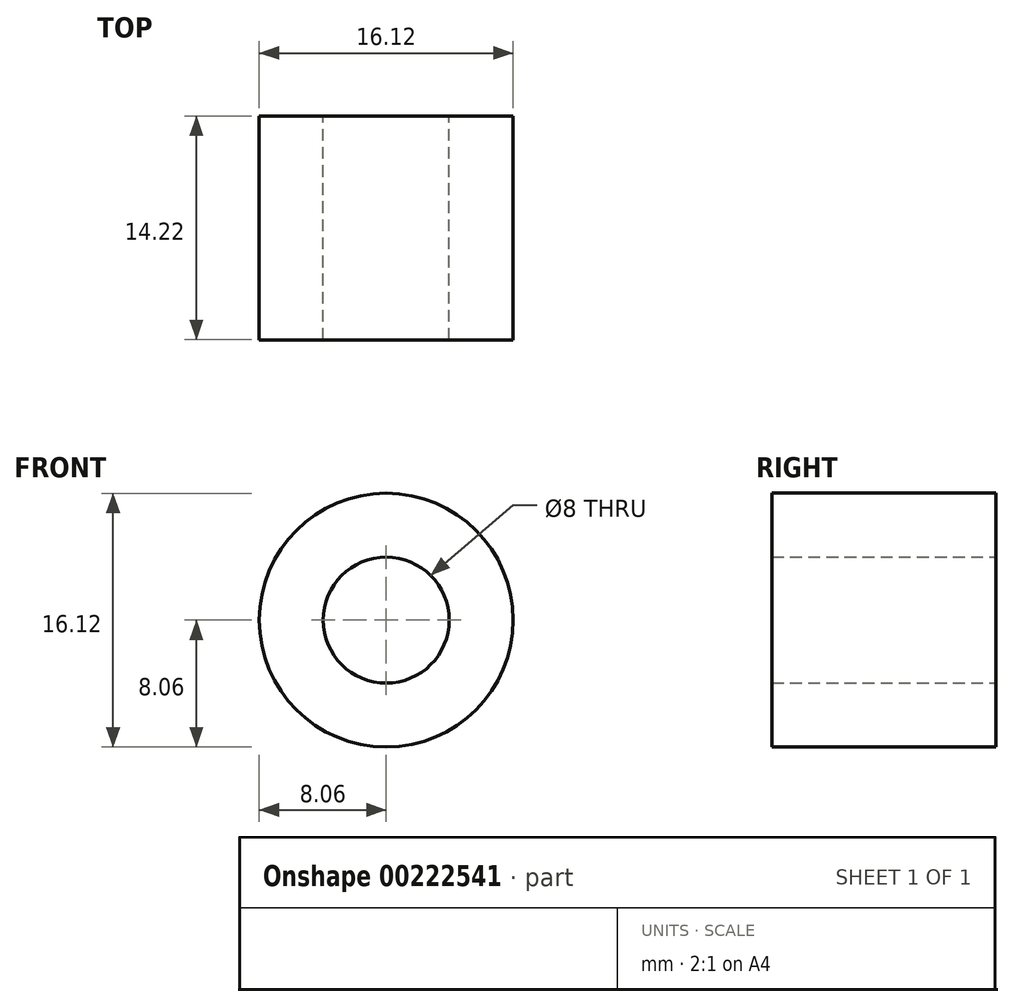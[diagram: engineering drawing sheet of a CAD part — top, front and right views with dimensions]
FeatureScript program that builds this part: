
annotation { "Feature Type Name" : "Feature", "Feature Type Description" : "" }
export const myFeature = defineFeature(function(context is Context, id is Id, definition is map)
    precondition{}
    {
        {
            var Q0;
            Q0=qCreatedBy(makeId("Front.planeOp"),FACE);
            var sketch = newSketch(context, id + "F0", { "sketchPlane" : qUnion([Q0])});
            skCircle(sketch, "E0", {"center": v(0, 0) * mm, "radius": 8.06 * mm});
            skCircle(sketch, "E1", {"center": v(0, 0) * mm, "radius": 4 * mm});
            skSolve(sketch);
        }
        {
            var Q0;
            Q0 = qSketchRegion(id + "F0", true);
            extrude(context, id + "F1", {"entities" : qUnion([Q0]), "depth" : 14.22 * mm});
        }
    });
